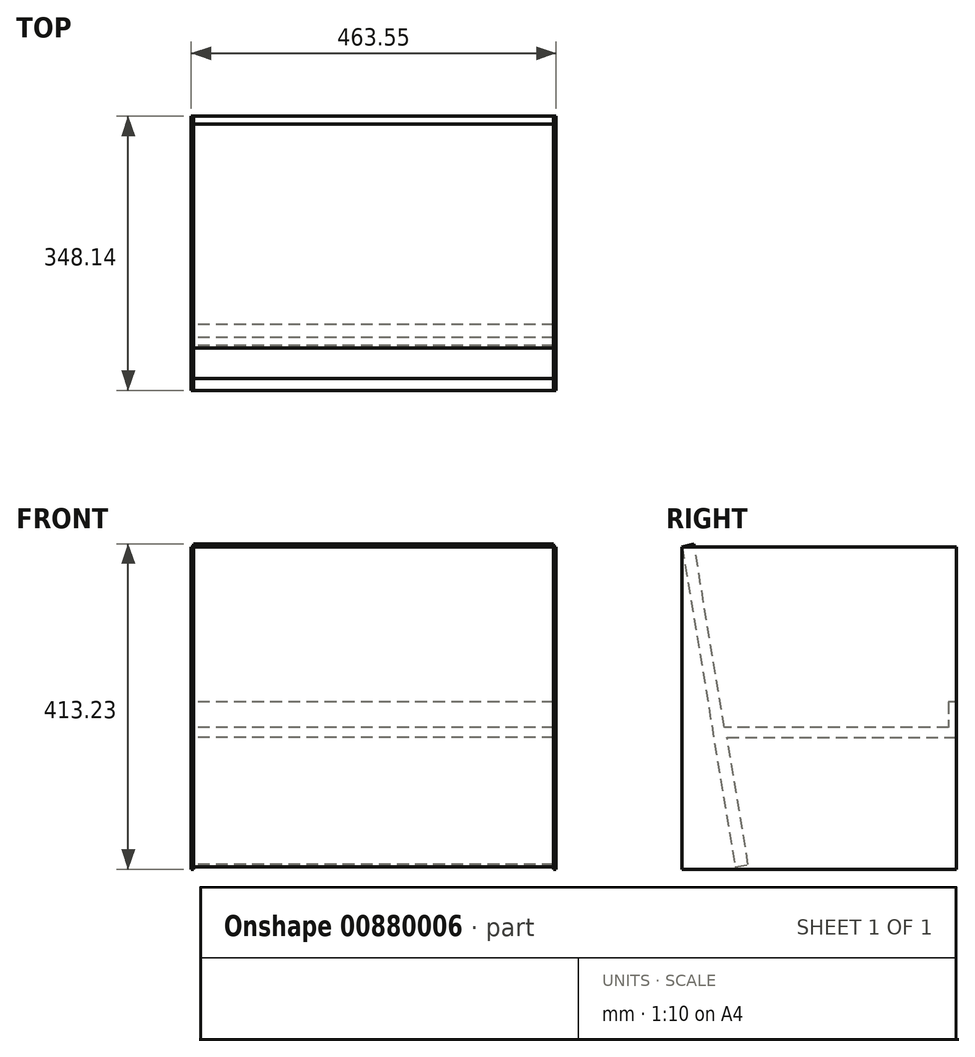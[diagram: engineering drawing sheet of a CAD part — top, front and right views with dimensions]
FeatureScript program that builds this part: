
annotation { "Feature Type Name" : "Feature", "Feature Type Description" : "" }
export const myFeature = defineFeature(function(context is Context, id is Id, definition is map)
    precondition{}
    {
        {
            var Q0;
            Q0=qCreatedBy(makeId("Right.planeOp"),FACE);
            var sketch = newSketch(context, id + "F0", { "sketchPlane" : qUnion([Q0])});
            skLineSegment(sketch, "E0", {"start": v(-186.6, 185.32) * mm, "end": v(-119.29, -221.08) * mm});
            skLineSegment(sketch, "E1", {"start": v(-119.29, -221.08) * mm, "end": v(-102.7, -218.33) * mm});
            skLineSegment(sketch, "E2", {"start": v(-102.7, -218.33) * mm, "end": v(-129.44, -56.91) * mm});
            skLineSegment(sketch, "E3", {"start": v(-129.44, -56.91) * mm, "end": v(161.53, -56.91) * mm});
            skLineSegment(sketch, "E4", {"start": v(161.53, -56.91) * mm, "end": v(161.53, -11.64) * mm});
            skLineSegment(sketch, "E5", {"start": v(161.53, -11.64) * mm, "end": v(151.83, -11.64) * mm});
            skLineSegment(sketch, "E6", {"start": v(151.83, -11.64) * mm, "end": v(151.83, -43.98) * mm});
            skLineSegment(sketch, "E7", {"start": v(151.83, -43.98) * mm, "end": v(-132.97, -43.98) * mm});
            skLineSegment(sketch, "E8", {"start": v(-132.97, -43.98) * mm, "end": v(-171.58, 189.08) * mm});
            skLineSegment(sketch, "E9", {"start": v(-171.58, 189.08) * mm, "end": v(-186.6, 185.32) * mm});
            skSolve(sketch);
        }
        {
            var Q0;
            Q0 = qSketchRegion(id + "F0", true);
            extrude(context, id + "F1", {"entities" : qUnion([Q0]), "depth" : 457.2 * mm, "offsetDistance" : 25.4 * mm});
        }
        {
            var Q0;
            Q0=makeQuery(id+"F1.opExtrude","CAP_FACE",FACE,{"disambiguationData":[OSD([sQuery(id+"F0.wireOp",EDGE,"E0"),sQuery(id+"F0.wireOp",EDGE,"E1"),sQuery(id+"F0.wireOp",EDGE,"E2"),sQuery(id+"F0.wireOp",EDGE,"E3"),sQuery(id+"F0.wireOp",EDGE,"E4"),sQuery(id+"F0.wireOp",EDGE,"E5"),sQuery(id+"F0.wireOp",EDGE,"E6"),sQuery(id+"F0.wireOp",EDGE,"E7"),sQuery(id+"F0.wireOp",EDGE,"E8"),sQuery(id+"F0.wireOp",EDGE,"E9")])],"isStart":false});
            var sketch = newSketch(context, id + "F2", { "sketchPlane" : qUnion([Q0])});
            skLineSegment(sketch, "E10.bottom", {"start": v(-186.6, 185.32) * mm, "end": v(161.53, 185.32) * mm});
            skLineSegment(sketch, "E10.top", {"start": v(-186.6, -224.15) * mm, "end": v(161.53, -224.15) * mm});
            skLineSegment(sketch, "E10.left", {"start": v(-186.6, 185.32) * mm, "end": v(-186.6, -224.15) * mm});
            skLineSegment(sketch, "E10.right", {"start": v(161.53, 185.32) * mm, "end": v(161.53, -224.15) * mm});
            skSolve(sketch);
        }
        {
            var Q0;
            Q0 = qSketchRegion(id + "F2", true);
            extrude(context, id + "F3", {"entities" : qUnion([Q0]), "operationType" : NewBodyOperationType.ADD, "depth" : 3.17 * mm, "offsetDistance" : 25.4 * mm});
        }
        {
            var Q0;
            Q0=makeQuery(id+"F1.opExtrude","CAP_FACE",FACE,{"disambiguationData":[OSD([sQuery(id+"F0.wireOp",EDGE,"E0"),sQuery(id+"F0.wireOp",EDGE,"E1"),sQuery(id+"F0.wireOp",EDGE,"E2"),sQuery(id+"F0.wireOp",EDGE,"E3"),sQuery(id+"F0.wireOp",EDGE,"E4"),sQuery(id+"F0.wireOp",EDGE,"E5"),sQuery(id+"F0.wireOp",EDGE,"E6"),sQuery(id+"F0.wireOp",EDGE,"E7"),sQuery(id+"F0.wireOp",EDGE,"E8"),sQuery(id+"F0.wireOp",EDGE,"E9")])],"isStart":true});
            var sketch = newSketch(context, id + "F4", { "sketchPlane" : qUnion([Q0])});
            skLineSegment(sketch, "E11.0", {"start": v(-161.53, -56.91) * mm, "end": v(-161.53, -224.15) * mm});
            skLineSegment(sketch, "E12.0", {"start": v(-161.53, 185.32) * mm, "end": v(-161.53, -11.64) * mm});
            skLineSegment(sketch, "E13.0", {"start": v(-161.53, 185.32) * mm, "end": v(-161.53, -224.15) * mm});
            skLineSegment(sketch, "E14.0", {"start": v(170.95, 185.32) * mm, "end": v(-161.53, 185.32) * mm});
            skLineSegment(sketch, "E15.0", {"start": v(186.6, -224.15) * mm, "end": v(-161.53, -224.15) * mm});
            skLineSegment(sketch, "E16.0", {"start": v(186.6, 185.32) * mm, "end": v(186.6, -224.15) * mm});
            skPoint(sketch, "E17.0", {"position": v(12.54, 185.32) * mm});
            skLineSegment(sketch, "E18.0", {"start": v(186.6, 185.32) * mm, "end": v(-161.53, 185.32) * mm});
            skSolve(sketch);
        }
        {
            var Q0;
            Q0 = qSketchRegion(id + "F4", true);
            extrude(context, id + "F5", {"entities" : qUnion([Q0]), "depth" : 3.17 * mm, "offsetDistance" : 25.4 * mm});
        }
    });
